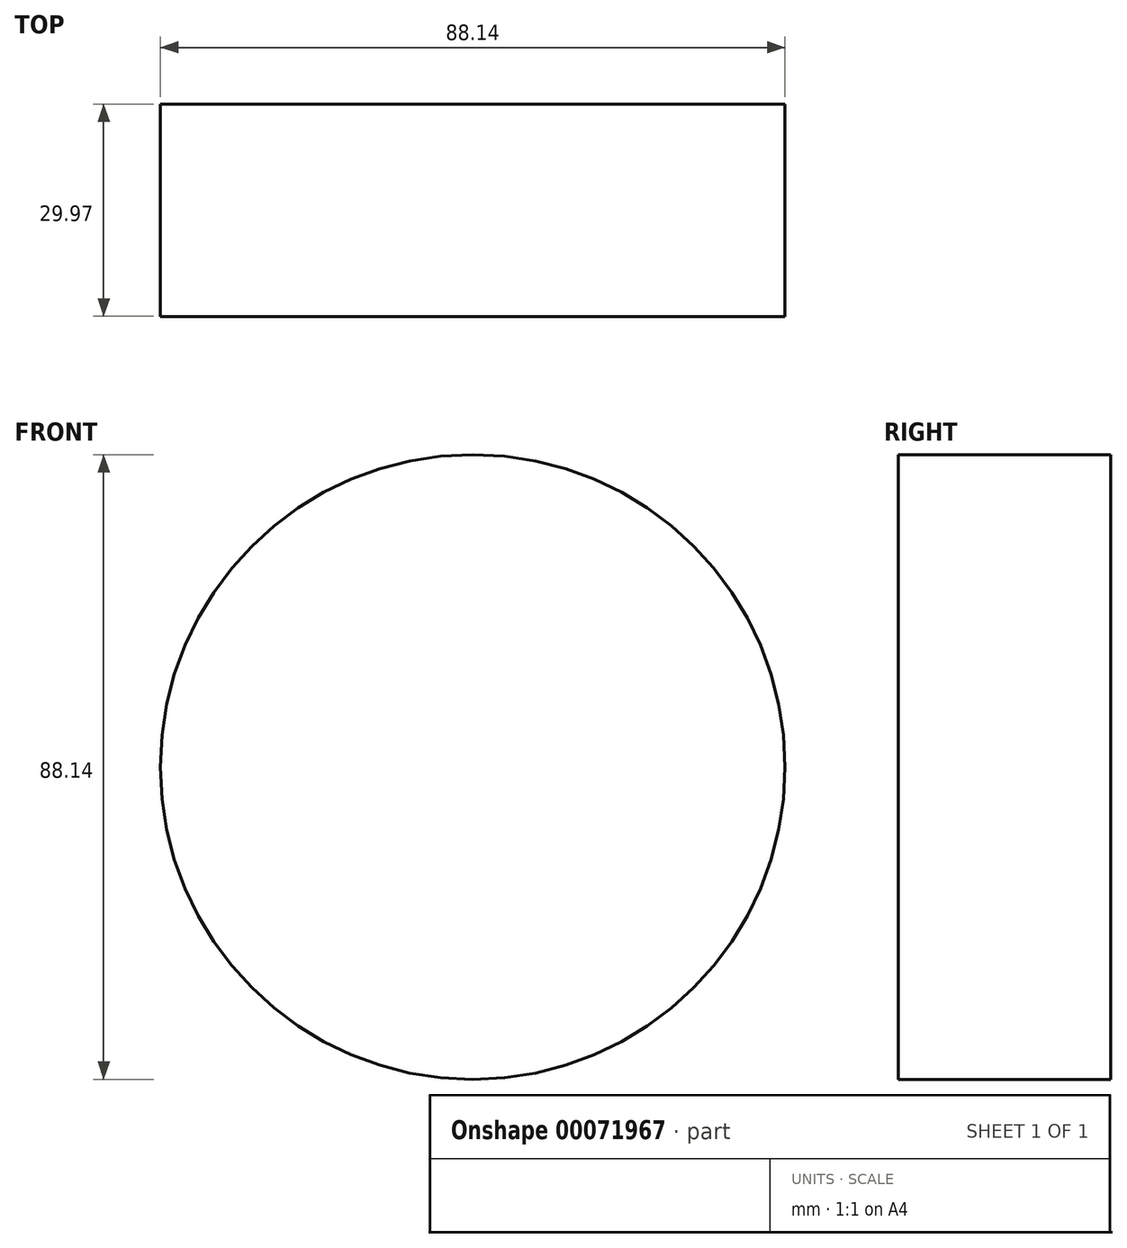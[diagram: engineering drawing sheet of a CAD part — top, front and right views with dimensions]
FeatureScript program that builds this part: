
annotation { "Feature Type Name" : "Feature", "Feature Type Description" : "" }
export const myFeature = defineFeature(function(context is Context, id is Id, definition is map)
    precondition{}
    {
        {
            var Q0;
            Q0=qCreatedBy(makeId("Front.planeOp"),FACE);
            var sketch = newSketch(context, id + "F0", { "sketchPlane" : qUnion([Q0])});
            skCircle(sketch, "E0", {"center": v(-8.3, 37.07) * mm, "radius": 44.07 * mm});
            skSolve(sketch);
        }
        {
            var Q0;
            Q0=makeQuery(id+"F0.imprint","IMPRINT",FACE,{"disambiguationData":[TD([[makeQuery(id+"F0.imprint","IMPRINT",EDGE,{"derivedFrom":sQuery(id+"F0.wireOp",EDGE,"E0")}),1.0]])]});
            extrude(context, id + "F1", {"entities" : qUnion([Q0]), "depth" : 29.97 * mm});
        }
    });
